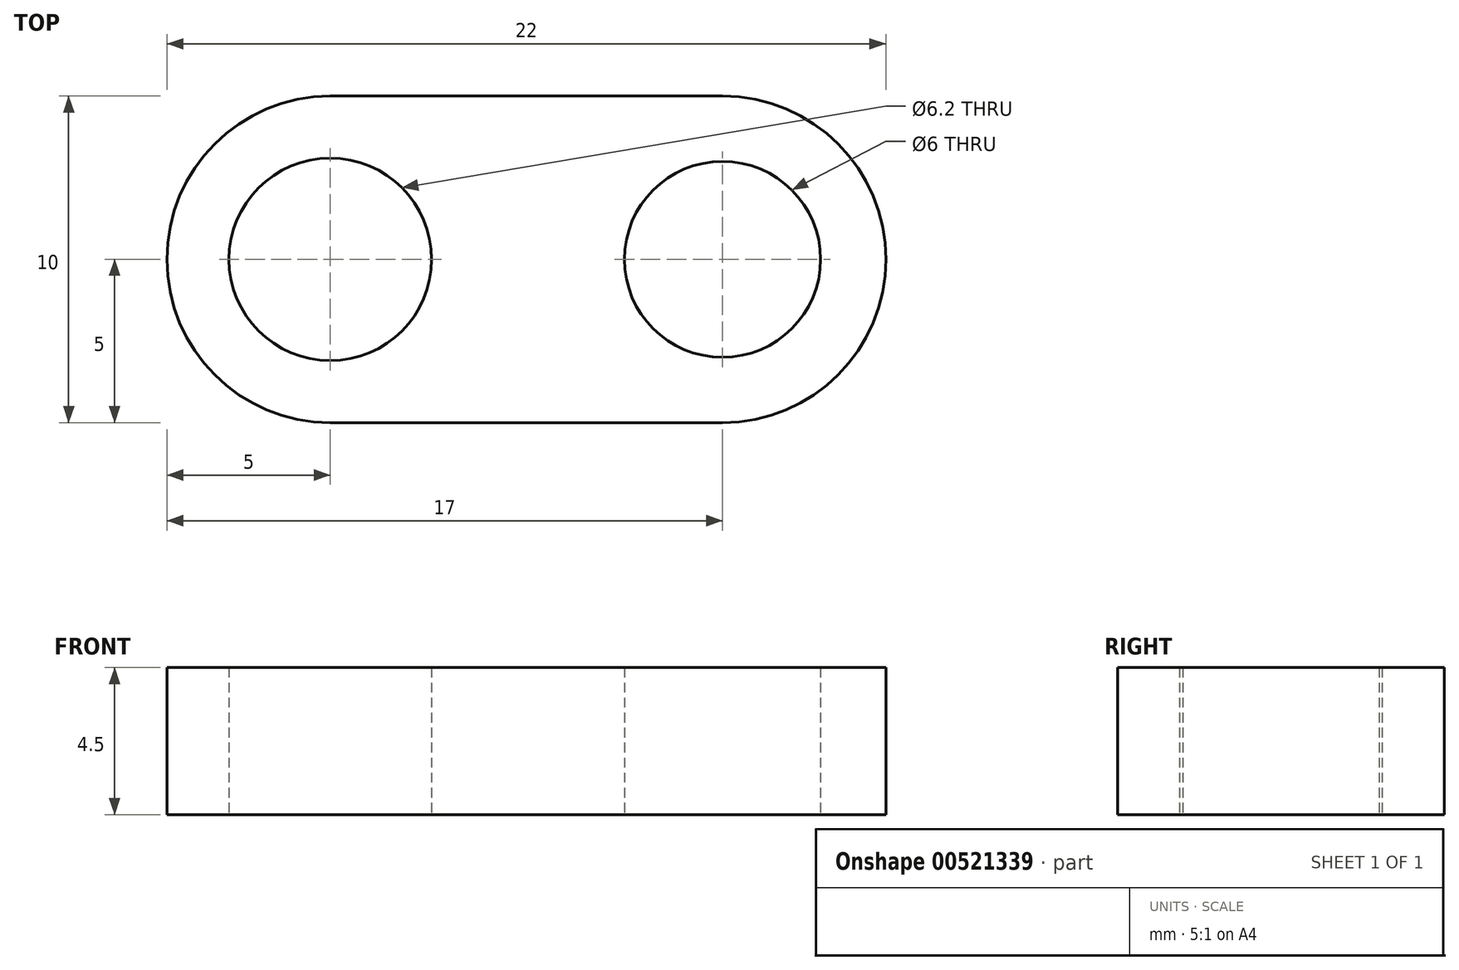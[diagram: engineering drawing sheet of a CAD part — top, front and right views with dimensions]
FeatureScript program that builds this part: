
annotation { "Feature Type Name" : "Feature", "Feature Type Description" : "" }
export const myFeature = defineFeature(function(context is Context, id is Id, definition is map)
    precondition{}
    {
        {
            var Q0;
            Q0=qCreatedBy(makeId("Top.planeOp"),FACE);
            var sketch = newSketch(context, id + "F0", { "sketchPlane" : qUnion([Q0])});
            skCircle(sketch, "E0", {"center": v(0, 0) * mm, "radius": 3.1 * mm});
            skArc(sketch, "E1", {"start": v(0, -5) * mm, "mid": v(-5, 0) * mm, "end": v(0, 5) * mm});
            skLineSegment(sketch, "E2", {"start": v(0, 5) * mm, "end": v(12, 5) * mm});
            skLineSegment(sketch, "E3", {"start": v(12, 5) * mm, "end": v(12, -5) * mm, "construction": true});
            skLineSegment(sketch, "E4", {"start": v(12, -5) * mm, "end": v(0, -5) * mm});
            skArc(sketch, "E5", {"start": v(12, 5) * mm, "mid": v(17, 0) * mm, "end": v(12, -5) * mm});
            skCircle(sketch, "E6", {"center": v(12, 0) * mm, "radius": 3 * mm});
            skSolve(sketch);
        }
        {
            var Q0;
            Q0 = qSketchRegion(id + "F0", true);
            extrude(context, id + "F1", {"entities" : qUnion([Q0]), "depth" : 4.5 * mm, "offsetDistance" : 25 * mm});
        }
    });
